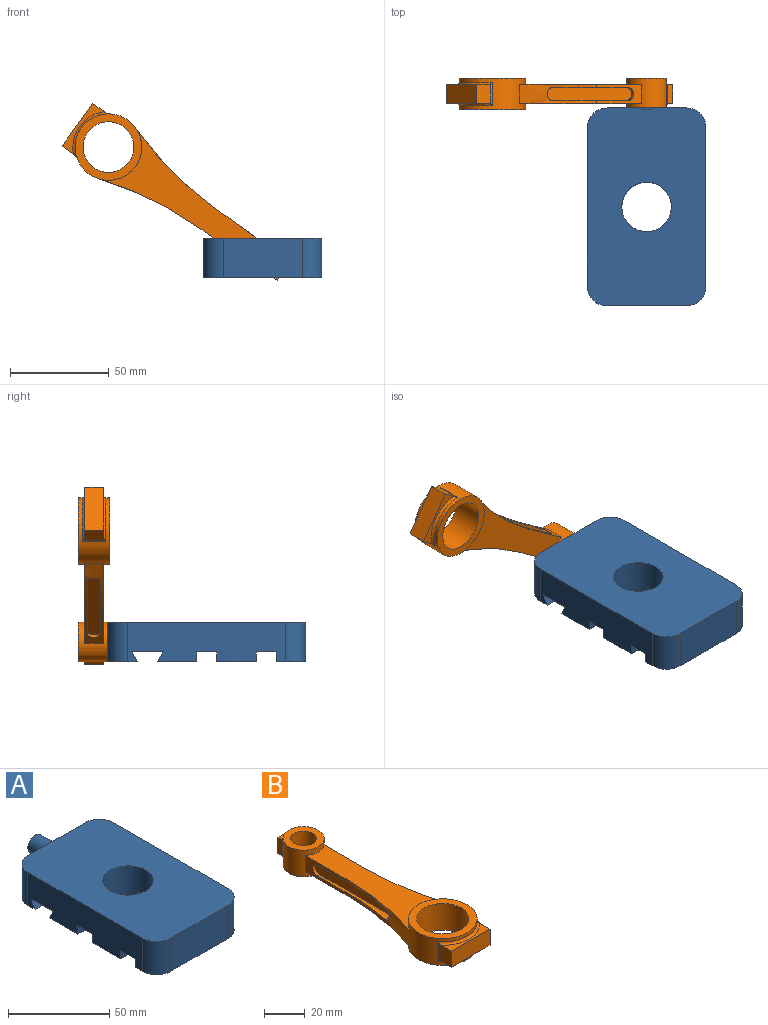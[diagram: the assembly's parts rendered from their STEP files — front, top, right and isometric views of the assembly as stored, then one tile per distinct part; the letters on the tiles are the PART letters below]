
ASSEMBLY  parts=2 mates=1
PART A: 28 faces, bbox 60x115x20 mm
  f0: plane 60x20mm, normal (0,0,-1), area 1076.1mm2, adj f1,f2,f6,f10,f16,f19
  f1: cylinder r=12.5mm len=25mm, axis (0,0,-1), area 1467.9mm2, adj f0,f4,f8,f10,f11,f12,f16,f17
  f2: plane 80x20mm, normal (1,0,0), area 1435.6mm2, adj f0,f3,f4,f8,f9,f10,f11,f12
  f3: plane 60x15mm, normal (0,0,-1), area 857.1mm2, adj f2,f6,f7,f13,f25,f26
  f4: plane 60x20mm, normal (0,0,-1), area 1076.1mm2, adj f1,f2,f6,f11,f14,f17
  f5: plane 40x20mm, normal (0,1,0), area 721.5mm2, adj f8,f9,f22,f24,f27
  f6: plane 80x20mm, normal (-1,0,0), area 1435.6mm2, adj f0,f3,f4,f8,f9,f13,f14,f15
  f7: plane 40x20mm, normal (0,-1,0), area 800mm2, adj f3,f8,f25,f26
  f8: plane 100x60mm, normal (0,0,1), area 5423.3mm2, adj f1,f2,f5,f6,f7,f24,f25,f26
  f9: plane 60x15mm, normal (0,0,-1), area 857.1mm2, adj f2,f5,f6,f20,f24,f27
  f10: plane 18.54x5mm, normal (0,-1,0), area 92.7mm2, adj f0,f1,f2,f12
  f11: plane 18.54x5mm, normal (0,1,0), area 92.7mm2, adj f1,f2,f4,f12
  f12: plane 18.54x10mm, normal (0,0,-1), area 178.4mm2, adj f1,f2,f10,f11
  f13: plane 60x5mm, normal (0,1,0), area 300mm2, adj f2,f3,f6,f15
  f14: plane 60x5mm, normal (0,-1,0), area 300mm2, adj f2,f4,f6,f15
  f15: plane 60x10mm, normal (0,0,-1), area 600mm2, adj f2,f6,f13,f14
  f16: plane 18.54x5mm, normal (0,-1,0), area 92.7mm2, adj f0,f1,f6,f18
  f17: plane 18.54x5mm, normal (0,1,0), area 92.7mm2, adj f1,f4,f6,f18
  f18: plane 18.54x10mm, normal (0,0,-1), area 178.4mm2, adj f1,f6,f16,f17
  f19: plane 60x5mm, normal (0,0.87,0.5), area 346.4mm2, adj f0,f2,f6,f21
  f20: plane 60x5mm, normal (0,-0.87,0.5), area 346.4mm2, adj f2,f6,f9,f21
  f21: plane 60x15.77mm, normal (0,0,-1), area 946.4mm2, adj f2,f6,f19,f20
  f22: cylinder r=5mm len=15mm, axis (0,-1,0), area 471.2mm2, adj f5,f23
  f23: plane 10x10mm, normal (0,1,0), area 78.5mm2, adj f22
  f24: cylinder r=10mm len=20mm, axis (0,0,1), area 314.2mm2, adj f5,f6,f8,f9
  f25: cylinder r=10mm len=20mm, axis (0,0,-1), area 314.2mm2, adj f3,f6,f7,f8
  f26: cylinder r=10mm len=20mm, axis (0,0,1), area 314.2mm2, adj f2,f3,f7,f8
  f27: cylinder r=10mm len=20mm, axis (0,0,-1), area 314.2mm2, adj f2,f5,f8,f9
PART B: 42 faces, bbox 33.7x129.5x16.1 mm
  f0: plane 82.69x31.66mm, normal (0,0,1), area 1120mm2, adj f6,f7,f8,f15,f31,f32
  f1: plane 82.69x31.66mm, normal (0,0,-1), area 1120mm2, adj f6,f7,f8,f15,f31,f32
  f2: plane 26.6x7.21mm, normal (0,0,1), area 83.7mm2, adj f9,f10,f27,f33
  f3: plane 10x2.64mm, normal (0,0,1), area 18.4mm2, adj f13,f14,f30,f34
  f4: plane 26.6x7.21mm, normal (0,0,-1), area 83.7mm2, adj f9,f10,f25,f33
  f5: plane 10x2.64mm, normal (0,0,-1), area 18.4mm2, adj f13,f14,f28,f34
  f6: plane 28x9.6mm, normal (-1,0,0), area 126.7mm2, adj f0,f1,f7,f15,f21,f22,f23
  f7: cylinder r=163.3mm len=54.69mm, axis (0,0,-1), area 326.4mm2, adj f0,f1,f6,f8,f21,f22,f24
  f8: cylinder r=16.8mm len=33.6mm, axis (0,0,-1), area 914.8mm2, adj f0,f1,f7,f16,f17,f25,f26,f27
  f9: plane 10.6x8.73mm, normal (-1,0,0), area 83.7mm2, adj f2,f4,f10,f25,f26,f27
  f10: plane 26.6x9.6mm, normal (0,-1,0), area 255.4mm2, adj f2,f4,f9,f33
  f11: cylinder r=12.8mm len=25.6mm, axis (0,0,-1), area 1286.8mm2, adj f16,f17
  f12: cylinder r=6.25mm len=16mm, axis (0,0,-1), area 628.3mm2, adj f18,f19
  f13: plane 10x9.6mm, normal (0,1,0), area 96mm2, adj f3,f5,f14,f34
  f14: plane 9.95x3.34mm, normal (-1,0,0), area 32.1mm2, adj f3,f5,f13,f28,f29,f30
  f15: cylinder r=10mm len=20mm, axis (0,0,-1), area 731.2mm2, adj f0,f1,f6,f18,f19,f28,f29,f30
  f16: plane 33.6x33.6mm, normal (0,0,-1), area 372mm2, adj f8,f11
  f17: plane 33.6x33.6mm, normal (0,0,1), area 372mm2, adj f8,f11
  f18: plane 20x20mm, normal (0,0,-1), area 191.4mm2, adj f12,f15
  f19: plane 20x20mm, normal (0,0,1), area 191.4mm2, adj f12,f15
  f20: plane 56x6.4mm, normal (-1,0,0), area 349.6mm2, adj f21,f22,f23,f24
  f21: plane 49.6x4.36mm, normal (0,0,1), area 106.8mm2, adj f6,f7,f20,f23,f24
  f22: plane 49.6x4.36mm, normal (0,0,-1), area 106.8mm2, adj f6,f7,f20,f23,f24
  f23: cylinder r=3.2mm len=6.4mm, axis (-1,0,0), area 16.1mm2, adj f6,f20,f21,f22
  f24: cylinder r=3.2mm len=6.4mm, axis (-1,0,0), area 47.8mm2, adj f7,f20,f21,f22
  f25: torus R=18mm, axis (0,0,1), area 57.5mm2, adj f4,f8,f9,f26,f33,f40
  f26: cylinder r=1.2mm len=12mm, axis (0,0,-1), area 8.6mm2, adj f8,f9,f25,f27
  f27: torus R=18mm, axis (0,0,1), area 57.5mm2, adj f2,f8,f9,f26,f33,f40
  f28: torus R=11.2mm, axis (0,0,1), area 20.3mm2, adj f5,f14,f15,f29,f34,f41
  f29: cylinder r=1.2mm len=12mm, axis (0,0,-1), area 13mm2, adj f14,f15,f28,f30
  f30: torus R=11.2mm, axis (0,0,1), area 20.3mm2, adj f3,f14,f15,f29,f34,f41
  f31: plane 28x9.6mm, normal (1,0,0), area 126.7mm2, adj f0,f1,f15,f32,f36,f37,f38
  f32: cylinder r=163.3mm len=54.69mm, axis (0,0,-1), area 326.4mm2, adj f0,f1,f8,f31,f36,f37,f39
  f33: plane 10.6x8.73mm, normal (1,0,0), area 83.7mm2, adj f2,f4,f10,f25,f27,f40
  f34: plane 9.95x3.34mm, normal (1,0,0), area 32.1mm2, adj f3,f5,f13,f28,f30,f41
  f35: plane 56x6.4mm, normal (1,0,0), area 349.6mm2, adj f36,f37,f38,f39
  f36: plane 49.6x4.36mm, normal (0,0,1), area 106.8mm2, adj f31,f32,f35,f38,f39
  f37: plane 49.6x4.36mm, normal (0,0,-1), area 106.8mm2, adj f31,f32,f35,f38,f39
  f38: cylinder r=3.2mm len=6.4mm, axis (1,0,0), area 16.1mm2, adj f31,f35,f36,f37
  f39: cylinder r=3.2mm len=6.4mm, axis (1,0,0), area 47.8mm2, adj f32,f35,f36,f37
  f40: cylinder r=1.2mm len=12mm, axis (0,0,-1), area 8.6mm2, adj f8,f25,f27,f33
  f41: cylinder r=1.2mm len=12mm, axis (0,0,-1), area 13mm2, adj f15,f28,f30,f34
PLACE A t=(-4.42,2.88,17.35)mm fixed
PLACE B rot(axis=(0.34,0.66,-0.66),142.4deg) t=(-82.37,59.88,83.39)mm
MATE revolute B.f12 <-> A.f22  axis (0,1,0) through (-4.42,67.88,27.35)mm
